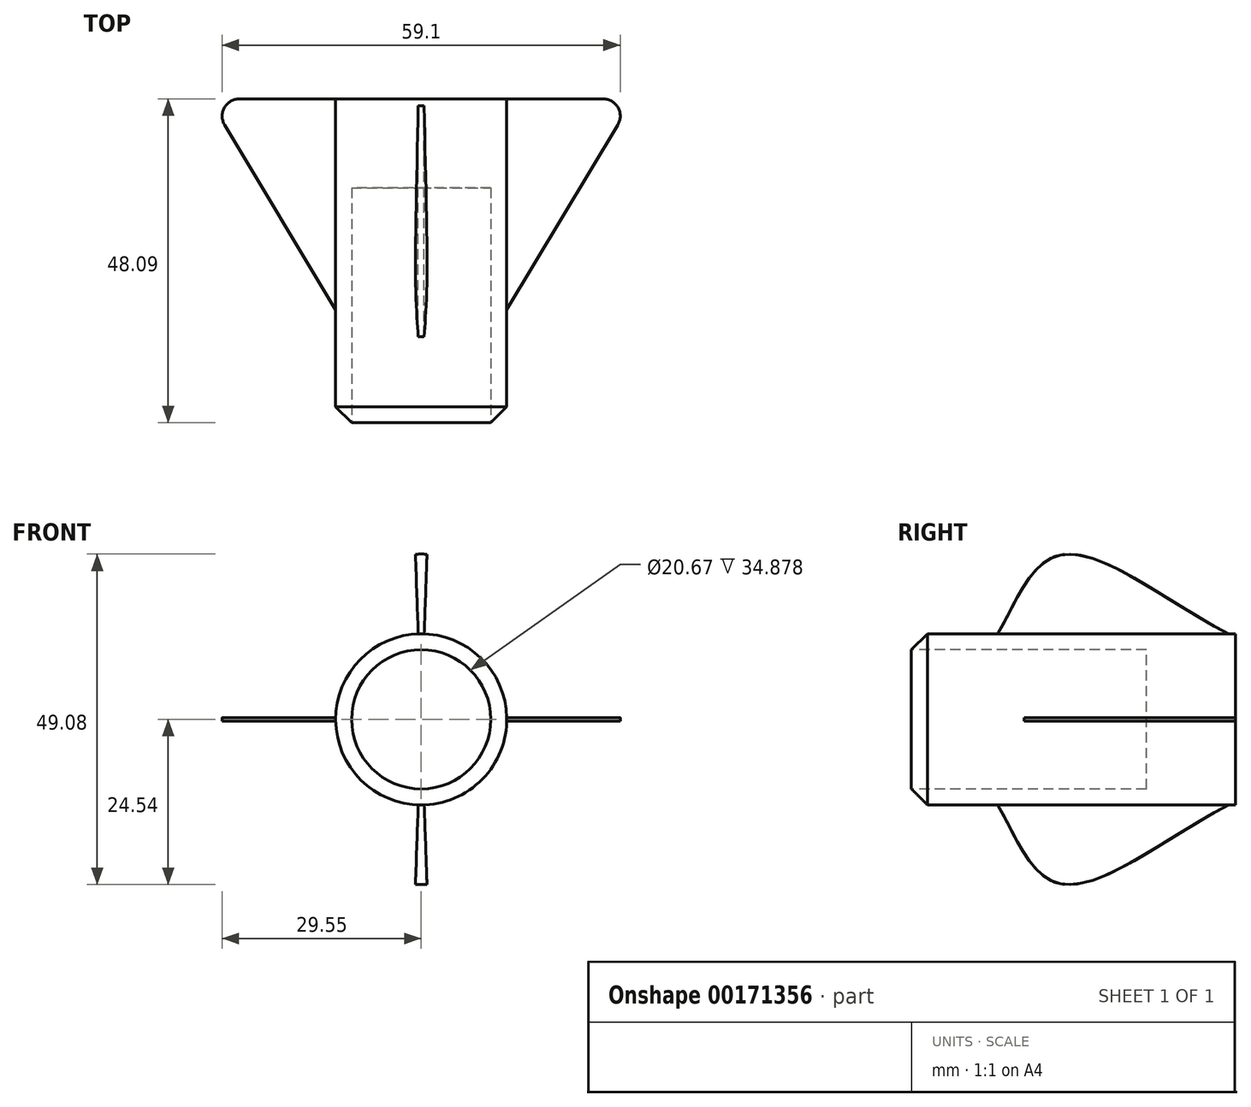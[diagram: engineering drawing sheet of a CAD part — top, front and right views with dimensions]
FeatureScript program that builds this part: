
annotation { "Feature Type Name" : "Feature", "Feature Type Description" : "" }
export const myFeature = defineFeature(function(context is Context, id is Id, definition is map)
    precondition{}
    {
        {
            var Q0;
            Q0=qCreatedBy(makeId("Front.planeOp"),FACE);
            var sketch = newSketch(context, id + "F0", { "sketchPlane" : qUnion([Q0])});
            skCircle(sketch, "E0", {"center": v(0, 0) * mm, "radius": 12.7 * mm});
            skSolve(sketch);
        }
        {
            var Q0;
            Q0=makeQuery(id+"F0.imprint","IMPRINT",FACE,{"disambiguationData":[TD([[makeQuery(id+"F0.imprint","IMPRINT",EDGE,{"derivedFrom":sQuery(id+"F0.wireOp",EDGE,"E0")}),1.0]])]});
            extrude(context, id + "F1", {"entities" : qUnion([Q0]), "depth" : 50.8 * mm});
        }
        {
            var Q0;
            Q0=makeQuery(id+"F1.opExtrude","CAP_FACE",FACE,{"disambiguationData":[OSD([sQuery(id+"F0.wireOp",EDGE,"E0")])],"isStart":false});
            var sketch = newSketch(context, id + "F2", { "sketchPlane" : qUnion([Q0])});
            skCircle(sketch, "E1", {"center": v(0, 0) * mm, "radius": 10.33 * mm});
            skSolve(sketch);
        }
        {
            var Q0;
            Q0=makeQuery(id+"F2.imprint","IMPRINT",FACE,{"disambiguationData":[TD([[makeQuery(id+"F2.imprint","IMPRINT",EDGE,{"derivedFrom":sQuery(id+"F2.wireOp",EDGE,"E1")}),1.0]])]});
            var Q1;
            Q1=makeQuery(id+"F1.opExtrude","CAP_FACE",FACE,{"disambiguationData":[OSD([sQuery(id+"F0.wireOp",EDGE,"E0")])],"isStart":true});
            extrude(context, id + "F3", {"entities" : qUnion([Q0]), "operationType" : NewBodyOperationType.REMOVE, "oppositeDirection" : true, "endBoundEntityFace" : qUnion([Q1]), "depth" : 37.6 * mm});
        }
        {
            var Q0;
            Q0=qCreatedBy(makeId("Right.planeOp"),FACE);
            var sketch = newSketch(context, id + "F4", { "sketchPlane" : qUnion([Q0])});
            skFitSpline(sketch, "E2", {"points": [v(-35.65, -12.2) * mm, v(-26.73, -24.21) * mm, v(0, -12.2) * mm], "startDerivative": vector(15.96, -21.58) * mm, "endDerivative": vector(51.01, 24.96) * mm});
            skLineSegment(sketch, "E3", {"start": v(-35.65, -12.2) * mm, "end": v(0, -12.2) * mm});
            skSolve(sketch);
        }
        {
            var Q0;
            Q0=qCreatedBy(makeId("Top.planeOp"),FACE);
            var sketch = newSketch(context, id + "F5", { "sketchPlane" : qUnion([Q0])});
            skLineSegment(sketch, "E4", {"start": v(-12.45, 0) * mm, "end": v(-31.5, 0) * mm});
            skLineSegment(sketch, "E5", {"start": v(-31.5, 0) * mm, "end": v(-12.45, -31.75) * mm});
            skLineSegment(sketch, "E6", {"start": v(-12.45, -31.75) * mm, "end": v(-12.45, 0) * mm});
            skLineSegment(sketch, "E7", {"start": v(20.2, 5.7) * mm, "end": v(24.67, -22.5) * mm});
            skSolve(sketch);
        }
        {
            var Q0;
            Q0=makeQuery(id+"F5.imprint","IMPRINT",FACE,{"disambiguationData":[TD([[makeQuery(id+"F5.imprint","IMPRINT",EDGE,{"derivedFrom":sQuery(id+"F5.wireOp",EDGE,"E4")}),1.0]])]});
            extrude(context, id + "F6", {"entities" : qUnion([Q0]), "endBound" : BoundingType.SYMMETRIC, "depth" : 0.5 * mm});
        }
        {
            var Q0;
            Q0=makeQuery(id+"F6.opExtrude","SWEPT_EDGE",EDGE,{"disambiguationData":[OSD([sQuery(id+"F5.wireOp",EDGE,"E4"),sQuery(id+"F5.wireOp",EDGE,"E5")])]});
            fillet(context, id + "F7", {"entities" : qUnion([Q0]), "radius" : 2.54 * mm, "allowEdgeOverflow" : false});
        }
        {
            var Q0;
            Q0=makeQuery(id+"F6.opExtrude","SWEPT_BODY",BODY,{"disambiguationData":[OSD([sQuery(id+"F5.wireOp",EDGE,"E4"),sQuery(id+"F5.wireOp",EDGE,"E5"),sQuery(id+"F5.wireOp",EDGE,"E6")])]});
            var Q1;
            Q1=qCreatedBy(makeId("Right.planeOp"),FACE);
            mirror(context, id + "F8", {"operationType" : NewBodyOperationType.ADD, "entities" : qUnion([Q0]), "mirrorPlane" : qUnion([Q1])});
        }
        {
            var Q0;
            Q0=makeQuery(id+"F4.imprint","IMPRINT",FACE,{"disambiguationData":[TD([[makeQuery(id+"F4.imprint","IMPRINT",EDGE,{"derivedFrom":sQuery(id+"F4.wireOp",EDGE,"E2")}),1.0]])]});
            var Q1;
            Q1=makeQuery(id+"F1.opExtrude","SWEPT_FACE",FACE,{"disambiguationData":[OSD([sQuery(id+"F0.wireOp",EDGE,"E0")])]});
            revolve(context, id + "F9", {"operationType" : NewBodyOperationType.ADD, "entities" : qUnion([Q0]), "axis" : qUnion([Q1]), "revolveType" : RevolveType.SYMMETRIC, "angle" : 4 * degree});
        }
        {
            var Q0;
            Q0=makeQuery(id+"F1.opExtrude","CAP_EDGE",EDGE,{"disambiguationData":[OSD([sQuery(id+"F0.wireOp",EDGE,"E0")])],"isStart":false});
            chamfer(context, id + "F10", {"entities" : qUnion([Q0]), "width" : 5.08 * mm, "tangentPropagation" : true});
        }
        {
            var Q0;
            Q0=makeQuery(id+"F1.opExtrude","SWEPT_BODY",BODY,{"disambiguationData":[OSD([sQuery(id+"F0.wireOp",EDGE,"E0")])]});
            var Q1;
            Q1=qCreatedBy(makeId("Top.planeOp"),FACE);
            mirror(context, id + "F11", {"operationType" : NewBodyOperationType.ADD, "entities" : qUnion([Q0]), "mirrorPlane" : qUnion([Q1])});
        }
    });
